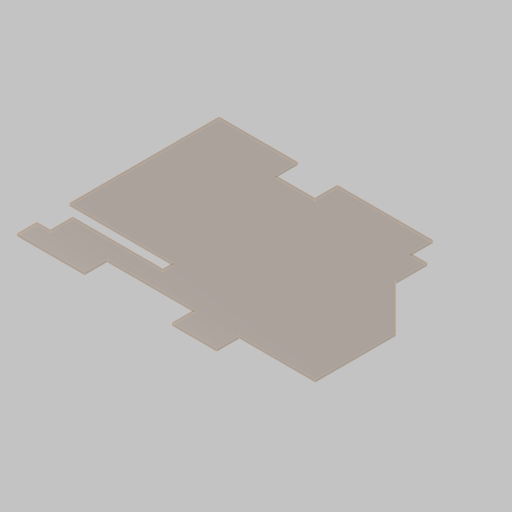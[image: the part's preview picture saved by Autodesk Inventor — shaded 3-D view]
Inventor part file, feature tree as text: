
AUTODESK INVENTOR PART (.ipt)
format: ipt  version: 2023.5 (Build 275446000, 446)  size: 287,744 bytes
history: native  units: in
note: dims shown in document units (in); Inventor stores cm internally (conversion verified against a paired STEP export)
features: sketch x6, projected_geometry x4, other x3, extrude x2, sheet_metal_op x1
ambient origin geometry x8: Origin, YZ Plane, XZ Plane, XY Plane, X Axis, Y Axis, Z Axis, Center Point
bodies: Solid1 (feature_tree)
feature tree (16):
  sheet_metal_op  "Face1"
  sketch  "Sketch3"  dims[d2=0.12in d3=8.25in]
  extrude  "Extrusion1"  Depth=28.0in
  extrude  "Extrusion2"  Depth=0.12in
  sketch  "Sketch1"  dims[d0=18.5in d1=28.0in]
  other  "Plate1"
  sketch  "Sketch4"  dims[d4=10.0in]
  projected_geometry  "Projected Loop1"
  sketch  "Sketch5"  dims[d5=45.0deg]
  sketch  "Sketch6"  dims[d6=2.4in]
  sketch  "Sketch7"  dims[d9=2.75in d10=0.12in d11=0.0in d12=45.0deg d13=8.25in d14=9.0in d15=2.75in d16=2.4in d17=6.75in d18=4.5in d19=0.25in d21=4.0in d22=1.0in d23=0.1in d26=5.7in d31=0.5in d32=4.5in d33=6.75in d34=0.25in d35=4.0in d36=1.0in d37=0.1in d38=3.0in d39=1.4in d40=1.7in d41=0.1in d42=1.0in d43=0.75in d44=1.0in d45=0.75in d46=0.75in d47=1.0in d48=0.75in d49=1.0in d50=0.12in d51=0.0in d52=1.75in d53=1.0in d54=3.5in d55=1.75in d56=1.0in d57=3.5in d58=1.0in d59=0.125in d60=3.0in d61=2.0in d62=11.0in d63=1.0in d64=0.0in d65=0.125in d66=0.125in d67=0.125in d68=0.125in d69=0.125in d70=0.125in d71=0.125in d72=0.125in d73=0.0625in d74=3.5in d75=0.0in d76=0.0in]
  other  "Cut1"
  other  "Cut2"
  projected_geometry  "Project Cut Edges1"
  projected_geometry  "Project Cut Edges2"
  projected_geometry  "Project Cut Edges3"
